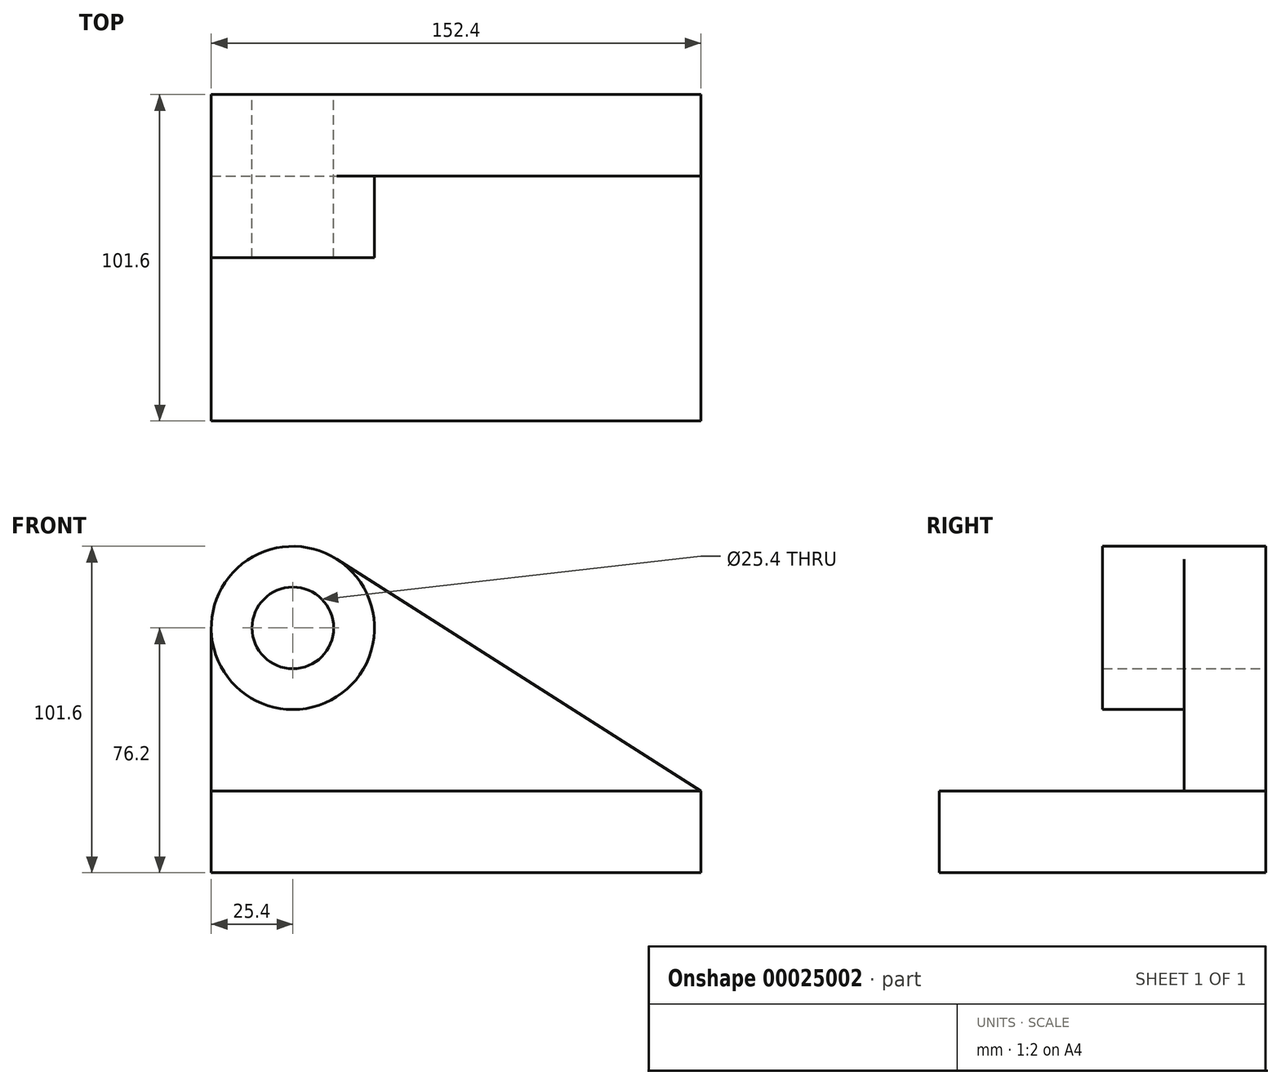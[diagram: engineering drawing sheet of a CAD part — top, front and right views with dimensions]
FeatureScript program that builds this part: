
annotation { "Feature Type Name" : "Feature", "Feature Type Description" : "" }
export const myFeature = defineFeature(function(context is Context, id is Id, definition is map)
    precondition{}
    {
        {
            var Q0;
            Q0=qCreatedBy(makeId("Front.planeOp"),FACE);
            var sketch = newSketch(context, id + "F0", { "sketchPlane" : qUnion([Q0])});
            skLineSegment(sketch, "E0", {"start": v(0, 0) * mm, "end": v(0, 76.2) * mm});
            skLineSegment(sketch, "E1", {"start": v(0, 0) * mm, "end": v(152.4, 0) * mm});
            skLineSegment(sketch, "E2", {"start": v(152.4, 0) * mm, "end": v(152.4, 25.4) * mm});
            skCircle(sketch, "E3", {"center": v(25.4, 76.2) * mm, "radius": 25.4 * mm});
            skCircle(sketch, "E4", {"center": v(25.4, 76.2) * mm, "radius": 12.7 * mm});
            skLineSegment(sketch, "E5", {"start": v(152.4, 25.4) * mm, "end": v(39.05, 97.62) * mm});
            skLineSegment(sketch, "E6", {"start": v(152.4, 25.4) * mm, "end": v(0, 25.4) * mm});
            skSolve(sketch);
        }
        {
            var Q0;
            {var subQ1=sQuery(id+"F0.wireOp",EDGE,"E5");Q0=makeQuery(id+"F0.imprint","IMPRINT",FACE,{"disambiguationData":[TD([[makeQuery(id+"F0.imprint","IMPRINT",EDGE,{"derivedFrom":subQ1}),1.0]])]});}
            extrude(context, id + "F1", {"entities" : qUnion([Q0]), "depth" : 25.4 * mm});
        }
        {
            var Q0;
            Q0=makeQuery(id+"F0.imprint","IMPRINT",FACE,{"disambiguationData":[TD([[makeQuery(id+"F0.imprint","IMPRINT",EDGE,{"derivedFrom":sQuery(id+"F0.wireOp",EDGE,"E4")}),-1.0]])]});
            extrude(context, id + "F2", {"entities" : qUnion([Q0]), "operationType" : NewBodyOperationType.ADD, "depth" : 50.8 * mm});
        }
        {
            var Q0;
            {var subQ1=sQuery(id+"F0.wireOp",EDGE,"E1");Q0=makeQuery(id+"F0.imprint","IMPRINT",FACE,{"disambiguationData":[TD([[makeQuery(id+"F0.imprint","IMPRINT",EDGE,{"derivedFrom":subQ1}),1.0]])]});}
            extrude(context, id + "F3", {"entities" : qUnion([Q0]), "operationType" : NewBodyOperationType.ADD, "depth" : 101.6 * mm});
        }
    });
